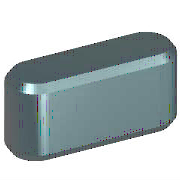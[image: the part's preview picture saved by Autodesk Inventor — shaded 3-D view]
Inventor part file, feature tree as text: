
AUTODESK INVENTOR PART (.ipt)
format: ipt  version: 2015 (Build 190159000, 159)  size: 135,680 bytes
history: native  units: mm (DEFAULTED — no unit token found)
features: plane x3, extrude x1
ambient origin geometry x8: Origin, YZ Plane, XZ Plane, XY Plane, X Axis, Y Axis, Z Axis, Center Point
bodies: Solid1 (feature_tree)
feature tree (4):
  plane  "Work Plane1"
  plane  "Work Plane2"
  extrude  "轴承体1"  Depth=3.0mm
  plane  "Work Plane3"
